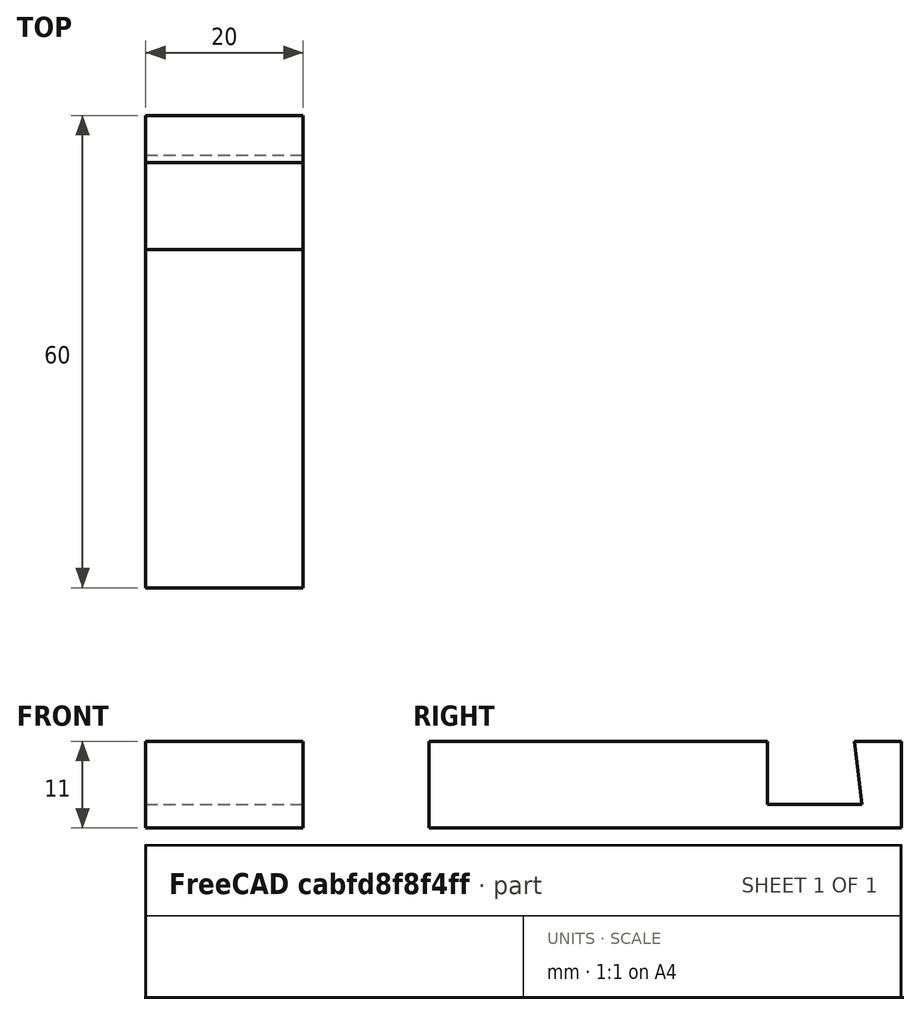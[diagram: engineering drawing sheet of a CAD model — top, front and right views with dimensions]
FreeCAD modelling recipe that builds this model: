
FCSTD DOCUMENT  (FreeCAD 0.21R33771 (Git))
Label: reto4
License: All rights reserved
LicenseURL: https://en.wikipedia.org/wiki/All_rights_reserved
objects: Sketcher::SketchObject×1, Part::Extrusion×1
note: 2 computed .brp shape members not serialized (recipe doc carries the construction recipe); baked Part::Feature solids carry a one-line shape summary decoded from their .brp

FEATURE [Sketcher::SketchObject] Sketch
  FullyConstrained = false
  Placement = pos=(0,0,0) rot=(0.57735,0.57735,0.57735;2.0944rad)
  sketch-geometry (8):
    g0: LineSegment StartX=0 StartY=0 StartZ=0 EndX=60.0035 EndY=0 EndZ=0
    g1: LineSegment StartX=0 StartY=0 StartZ=0 EndX=0 EndY=11.0008 EndZ=0
    g2: LineSegment StartX=60.0035 StartY=0 StartZ=0 EndX=60.0035 EndY=11.0008 EndZ=0
    g3: LineSegment StartX=42.9994 StartY=2.99996 StartZ=0 EndX=55.0092 EndY=2.99996 EndZ=0
    g4: LineSegment StartX=54.0025 StartY=11.0008 StartZ=0 EndX=55.0092 EndY=2.99996 EndZ=0
    g5: LineSegment StartX=42.9994 StartY=11.0008 StartZ=0 EndX=0 EndY=11.0008 EndZ=0
    g6: LineSegment StartX=54.0025 StartY=11.0008 StartZ=0 EndX=60.0035 EndY=11.0008 EndZ=0
    g7: LineSegment StartX=42.9994 StartY=11.0008 StartZ=0 EndX=42.9994 EndY=2.99996 EndZ=0
  constraints (13):
    c: Coincident(g0,g-1)
    c: PointOnObject(g0,g-1)
    c: Coincident(g1,g0)
    c: PointOnObject(g1,g-2)
    c: Coincident(g2,g0)
    c: Vertical(g2)
    c: Horizontal(g3)
    c: Coincident(g4,g3)
    c: Coincident(g5,g1)
    c: Horizontal(g5)
    c: Coincident(g6,g2)
    c: Horizontal(g6)
    c: Vertical(g7)
FEATURE [Part::Extrusion] Extrude
  Base = -> Sketch
  Dir = (1,0,0)
  DirMode = 2
  FaceMakerClass = Part::FaceMakerBullseye
  LengthFwd = 20
  LengthRev = 0
  Solid = true
  Symmetric = false
